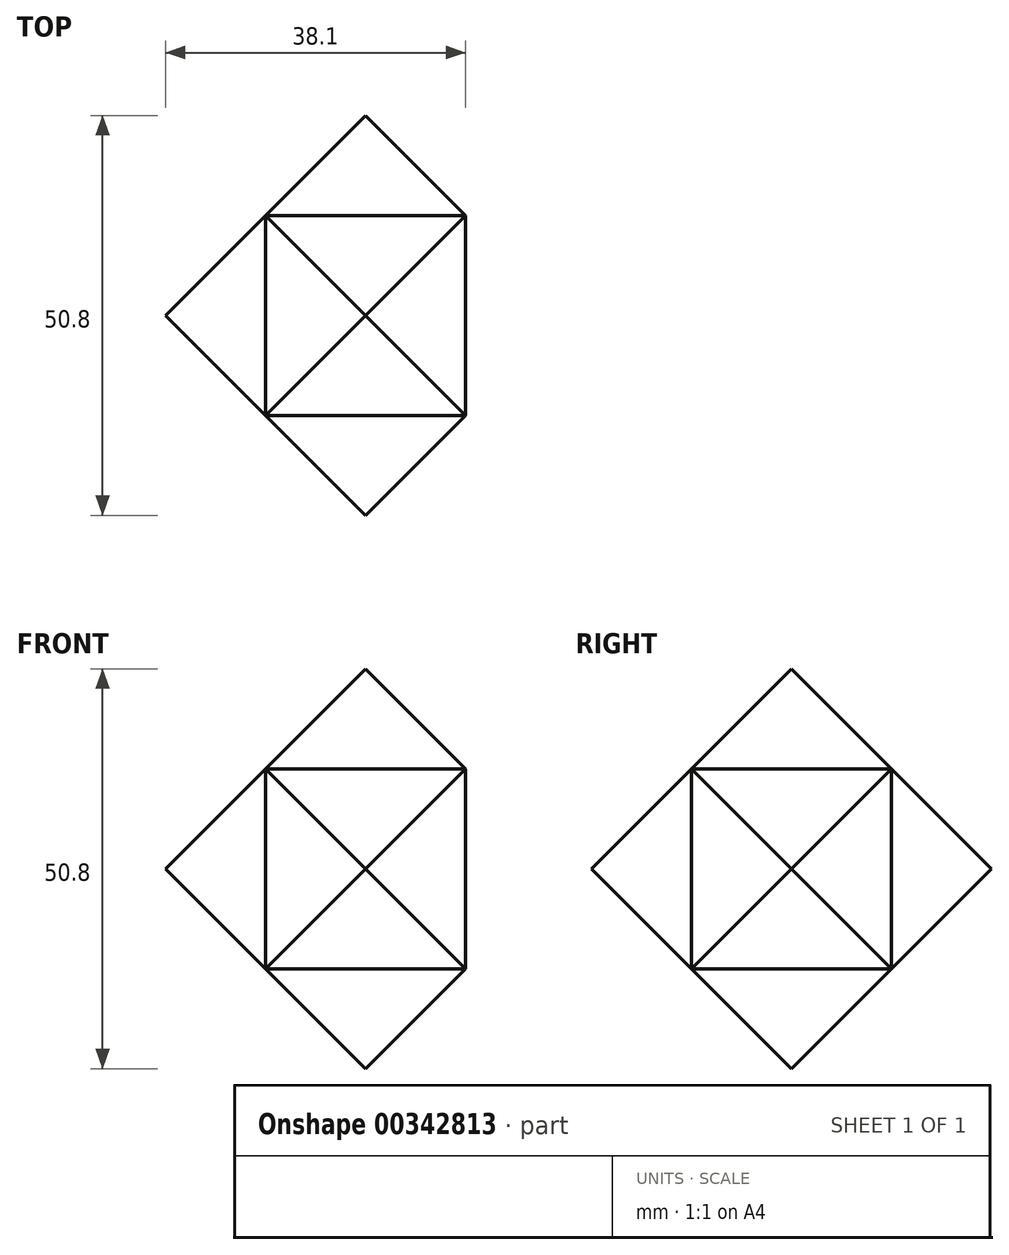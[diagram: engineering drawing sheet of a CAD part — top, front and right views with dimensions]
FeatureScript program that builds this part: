
annotation { "Feature Type Name" : "Feature", "Feature Type Description" : "" }
export const myFeature = defineFeature(function(context is Context, id is Id, definition is map)
    precondition{}
    {
        {
            var Q0;
            Q0=qCreatedBy(makeId("Top.planeOp"),FACE);
            var sketch = newSketch(context, id + "F0", { "sketchPlane" : qUnion([Q0])});
            skLineSegment(sketch, "E0.bottom", {"start": v(12.7, -12.7) * mm, "end": v(-12.7, -12.7) * mm});
            skLineSegment(sketch, "E0.top", {"start": v(12.7, 12.7) * mm, "end": v(-12.7, 12.7) * mm});
            skLineSegment(sketch, "E0.left", {"start": v(12.7, -12.7) * mm, "end": v(12.7, 12.7) * mm});
            skLineSegment(sketch, "E0.right", {"start": v(-12.7, -12.7) * mm, "end": v(-12.7, 12.7) * mm});
            skPoint(sketch, "E0.middle", {"position": v(0, 0) * mm});
            skSolve(sketch);
        }
        {
            var Q0;
            Q0=makeQuery(id+"F0.imprint","IMPRINT",FACE,{"disambiguationData":[TD([[makeQuery(id+"F0.imprint","IMPRINT",EDGE,{"derivedFrom":sQuery(id+"F0.wireOp",EDGE,"E0.bottom")}),-1.0]])]});
            extrude(context, id + "F1", {"entities" : qUnion([Q0]), "endBound" : BoundingType.SYMMETRIC, "depth" : 2.54 * mm});
        }
        {
            var Q0;
            Q0=makeQuery(id+"F1.opExtrude","SWEPT_FACE",FACE,{"disambiguationData":[OSD([sQuery(id+"F0.wireOp",EDGE,"E0.left")])]});
            var sketch = newSketch(context, id + "F2", { "sketchPlane" : qUnion([Q0])});
            skLineSegment(sketch, "E1.bottom", {"start": v(12.7, -12.7) * mm, "end": v(-12.7, -12.7) * mm});
            skLineSegment(sketch, "E1.top", {"start": v(12.7, 12.7) * mm, "end": v(-12.7, 12.7) * mm});
            skLineSegment(sketch, "E1.left", {"start": v(12.7, -12.7) * mm, "end": v(12.7, 12.7) * mm});
            skLineSegment(sketch, "E1.right", {"start": v(-12.7, -12.7) * mm, "end": v(-12.7, 12.7) * mm});
            skPoint(sketch, "E1.middle", {"position": v(0, 0) * mm});
            skSolve(sketch);
        }
        {
            var Q0;
            {var subQ0=sQuery(id+"F2.wireOp",EDGE,"E1.top");Q0=makeQuery(id+"F2.imprint","IMPRINT",FACE,{"disambiguationData":[TD([[makeQuery(id+"F2.imprint","IMPRINT",EDGE,{"derivedFrom":subQ0}),1.0]])]});}
            var Q1;
            {var subQ1=sQuery(id+"F0.wireOp",EDGE,"E0.left");var subQ2=makeQuery(id+"F1.opExtrude","CAP_EDGE",EDGE,{"disambiguationData":[OSD([subQ1])],"isStart":true});Q1=makeQuery(id+"F2.imprint","IMPRINT",FACE,{"disambiguationData":[TD([[makeQuery(id+"F2.imprint","IMPRINT",EDGE,{"derivedFrom":subQ2}),1.0]])]});}
            var Q2;
            {var subQ0=sQuery(id+"F2.wireOp",EDGE,"E1.bottom");Q2=makeQuery(id+"F2.imprint","IMPRINT",FACE,{"disambiguationData":[TD([[makeQuery(id+"F2.imprint","IMPRINT",EDGE,{"derivedFrom":subQ0}),-1.0]])]});}
            var Q3;
            Q3=makeQuery(id+"F1.opExtrude","SWEPT_FACE",FACE,{"disambiguationData":[OSD([sQuery(id+"F0.wireOp",EDGE,"E0.right")])]});
            extrude(context, id + "F3", {"entities" : qUnion([Q0, Q1, Q2]), "operationType" : NewBodyOperationType.ADD, "endBound" : BoundingType.UP_TO_SURFACE, "oppositeDirection" : true, "endBoundEntityFace" : qUnion([Q3]), "depth" : 25.4 * mm});
        }
        {
            var Q0;
            Q0=makeQuery(id+"F3.opExtrude","SWEPT_EDGE",EDGE,{"disambiguationData":[OSD([sQuery(id+"F2.wireOp",EDGE,"E1.top"),sQuery(id+"F2.wireOp",EDGE,"E1.right")])]});
            var Q1;
            {var subQ0=sQuery(id+"F2.wireOp",EDGE,"E1.right");var subQ1=sQuery(id+"F0.wireOp",EDGE,"E0.left");var subQ2=makeQuery(id+"F2.imprint","INTERSECT",VERTEX,{"derivedFrom":[makeQuery(id+"F1.opExtrude","CAP_EDGE",EDGE,{"disambiguationData":[OSD([subQ1])],"isStart":false}),subQ0]});var subQ3=makeQuery(id+"F2.imprint","INTERSECT",VERTEX,{"derivedFrom":[makeQuery(id+"F1.opExtrude","CAP_EDGE",EDGE,{"disambiguationData":[OSD([subQ1])],"isStart":true}),subQ0]});var subQ4=sQuery(id+"F0.wireOp",EDGE,"E0.right");Q1=makeQuery(id+"F3.boolean.opBoolean","MERGE",EDGE,{"derivedFrom":[makeQuery(id+"F1.opExtrude","SWEPT_EDGE",EDGE,{"disambiguationData":[OSD([sQuery(id+"F0.wireOp",EDGE,"E0.bottom"),subQ4])]}),makeQuery(id+"F3.opExtrude","TWEAK_EDGE",EDGE,{"derivedFrom":[makeQuery(id+"F1.opExtrude","SWEPT_FACE",FACE,{"disambiguationData":[OSD([subQ4])]}),makeQuery(id+"F2.imprint","IMPRINT",EDGE,{"disambiguationData":[TD([[subQ3,1.0],[makeQuery(id+"F2.imprint","INTERSECT",VERTEX,{"derivedFrom":[sQuery(id+"F2.wireOp",EDGE,"E1.bottom"),subQ0]}),-1.0]])],"derivedFrom":subQ0}),makeQuery(id+"F2.imprint","IMPRINT",EDGE,{"disambiguationData":[TD([[subQ3,1.0],[subQ2,-1.0]])],"derivedFrom":subQ0}),makeQuery(id+"F2.imprint","IMPRINT",EDGE,{"disambiguationData":[TD([[subQ2,-1.0],[makeQuery(id+"F2.imprint","INTERSECT",VERTEX,{"derivedFrom":[sQuery(id+"F2.wireOp",EDGE,"E1.top"),subQ0]}),1.0]])],"derivedFrom":subQ0})]})]});}
            var Q2;
            Q2=makeQuery(id+"F3.boolean.opBoolean","MERGE",EDGE,{"derivedFrom":[makeQuery(id+"F1.opExtrude","SWEPT_EDGE",EDGE,{"disambiguationData":[OSD([sQuery(id+"F0.wireOp",EDGE,"E0.bottom"),sQuery(id+"F0.wireOp",EDGE,"E0.left")])]}),makeQuery(id+"F3.opExtrude","CAP_EDGE",EDGE,{"disambiguationData":[OSD([sQuery(id+"F2.wireOp",EDGE,"E1.right")])],"isStart":true})]});
            var Q3;
            Q3=makeQuery(id+"F3.boolean.opBoolean","MERGE",EDGE,{"derivedFrom":[makeQuery(id+"F1.opExtrude","SWEPT_EDGE",EDGE,{"disambiguationData":[OSD([sQuery(id+"F0.wireOp",EDGE,"E0.top"),sQuery(id+"F0.wireOp",EDGE,"E0.left")])]}),makeQuery(id+"F3.opExtrude","CAP_EDGE",EDGE,{"disambiguationData":[OSD([sQuery(id+"F2.wireOp",EDGE,"E1.left")])],"isStart":true})]});
            var Q4;
            Q4=makeQuery(id+"F3.opExtrude","SWEPT_EDGE",EDGE,{"disambiguationData":[OSD([sQuery(id+"F2.wireOp",EDGE,"E1.bottom"),sQuery(id+"F2.wireOp",EDGE,"E1.right")])]});
            var Q5;
            Q5=makeQuery(id+"F3.opExtrude","SWEPT_EDGE",EDGE,{"disambiguationData":[OSD([sQuery(id+"F2.wireOp",EDGE,"E1.top"),sQuery(id+"F2.wireOp",EDGE,"E1.left")])]});
            var Q6;
            Q6=makeQuery(id+"F3.opExtrude","SWEPT_EDGE",EDGE,{"disambiguationData":[OSD([sQuery(id+"F2.wireOp",EDGE,"E1.bottom"),sQuery(id+"F2.wireOp",EDGE,"E1.left")])]});
            var Q7;
            {var subQ0=sQuery(id+"F2.wireOp",EDGE,"E1.left");var subQ1=sQuery(id+"F0.wireOp",EDGE,"E0.left");var subQ2=makeQuery(id+"F2.imprint","INTERSECT",VERTEX,{"derivedFrom":[makeQuery(id+"F1.opExtrude","CAP_EDGE",EDGE,{"disambiguationData":[OSD([subQ1])],"isStart":false}),subQ0]});var subQ3=makeQuery(id+"F2.imprint","INTERSECT",VERTEX,{"derivedFrom":[makeQuery(id+"F1.opExtrude","CAP_EDGE",EDGE,{"disambiguationData":[OSD([subQ1])],"isStart":true}),subQ0]});var subQ4=sQuery(id+"F0.wireOp",EDGE,"E0.right");Q7=makeQuery(id+"F3.boolean.opBoolean","MERGE",EDGE,{"derivedFrom":[makeQuery(id+"F1.opExtrude","SWEPT_EDGE",EDGE,{"disambiguationData":[OSD([sQuery(id+"F0.wireOp",EDGE,"E0.top"),subQ4])]}),makeQuery(id+"F3.opExtrude","TWEAK_EDGE",EDGE,{"derivedFrom":[makeQuery(id+"F1.opExtrude","SWEPT_FACE",FACE,{"disambiguationData":[OSD([subQ4])]}),makeQuery(id+"F2.imprint","IMPRINT",EDGE,{"disambiguationData":[TD([[subQ3,1.0],[makeQuery(id+"F2.imprint","INTERSECT",VERTEX,{"derivedFrom":[sQuery(id+"F2.wireOp",EDGE,"E1.bottom"),subQ0]}),-1.0]])],"derivedFrom":subQ0}),makeQuery(id+"F2.imprint","IMPRINT",EDGE,{"disambiguationData":[TD([[subQ3,1.0],[subQ2,-1.0]])],"derivedFrom":subQ0}),makeQuery(id+"F2.imprint","IMPRINT",EDGE,{"disambiguationData":[TD([[subQ2,-1.0],[makeQuery(id+"F2.imprint","INTERSECT",VERTEX,{"derivedFrom":[sQuery(id+"F2.wireOp",EDGE,"E1.top"),subQ0]}),1.0]])],"derivedFrom":subQ0})]})]});}
            chamfer(context, id + "F4", {"entities" : qUnion([Q0, Q1, Q2, Q3, Q4, Q5, Q6, Q7]), "width" : 12.7 * mm, "tangentPropagation" : true});
        }
        {
            var Q0;
            Q0=makeQuery(id+"F1.opExtrude","SWEPT_BODY",BODY,{"disambiguationData":[OSD([sQuery(id+"F0.wireOp",EDGE,"E0.bottom"),sQuery(id+"F0.wireOp",EDGE,"E0.top"),sQuery(id+"F0.wireOp",EDGE,"E0.left"),sQuery(id+"F0.wireOp",EDGE,"E0.right")])]});
            var Q1;
            {var subQ0=sQuery(id+"F2.wireOp",EDGE,"E1.left");Q1=makeQuery(id+"F4.opChamfer","BLEND_EDGE",EDGE,{"blendedFrom":[makeQuery(id+"F3.opExtrude","SWEPT_EDGE",EDGE,{"disambiguationData":[OSD([sQuery(id+"F2.wireOp",EDGE,"E1.top"),subQ0])]}),makeQuery(id+"F3.boolean.opBoolean","MERGE",EDGE,{"derivedFrom":[makeQuery(id+"F1.opExtrude","SWEPT_EDGE",EDGE,{"disambiguationData":[OSD([sQuery(id+"F0.wireOp",EDGE,"E0.top"),sQuery(id+"F0.wireOp",EDGE,"E0.left")])]}),makeQuery(id+"F3.opExtrude","CAP_EDGE",EDGE,{"disambiguationData":[OSD([subQ0])],"isStart":true})]})],"blendedInto":[]});}
            transform(context, id + "F5", {"entities" : qUnion([Q0]), "transformType" : TransformType.ROTATION, "transformAxis" : qUnion([Q1]), "angle" : 120 * degree, "makeCopy" : true});
        }
        {
            var Q0;
            Q0=makeQuery(id+"F1.opExtrude","SWEPT_BODY",BODY,{"disambiguationData":[OSD([sQuery(id+"F0.wireOp",EDGE,"E0.bottom"),sQuery(id+"F0.wireOp",EDGE,"E0.top"),sQuery(id+"F0.wireOp",EDGE,"E0.left"),sQuery(id+"F0.wireOp",EDGE,"E0.right")])]});
            var Q1;
            Q1=makeQuery(id+"F5.opPattern","COPY",BODY,{"derivedFrom":makeQuery(id+"F1.opExtrude","SWEPT_BODY",BODY,{"disambiguationData":[OSD([sQuery(id+"F0.wireOp",EDGE,"E0.bottom"),sQuery(id+"F0.wireOp",EDGE,"E0.top"),sQuery(id+"F0.wireOp",EDGE,"E0.left"),sQuery(id+"F0.wireOp",EDGE,"E0.right")])]}),"instanceName":"1"});
            var Q2;
            {var subQ0=sQuery(id+"F2.wireOp",EDGE,"E1.left");var subQ1=sQuery(id+"F0.wireOp",EDGE,"E0.left");var subQ2=makeQuery(id+"F2.imprint","INTERSECT",VERTEX,{"derivedFrom":[makeQuery(id+"F1.opExtrude","CAP_EDGE",EDGE,{"disambiguationData":[OSD([subQ1])],"isStart":false}),subQ0]});var subQ3=sQuery(id+"F2.wireOp",EDGE,"E1.top");var subQ4=makeQuery(id+"F2.imprint","INTERSECT",VERTEX,{"derivedFrom":[makeQuery(id+"F1.opExtrude","CAP_EDGE",EDGE,{"disambiguationData":[OSD([subQ1])],"isStart":true}),subQ0]});var subQ5=sQuery(id+"F0.wireOp",EDGE,"E0.right");Q2=makeQuery(id+"F5.opPattern","COPY",EDGE,{"derivedFrom":makeQuery(id+"F4.opChamfer","BLEND_EDGE",EDGE,{"blendedFrom":[makeQuery(id+"F3.opExtrude","SWEPT_EDGE",EDGE,{"disambiguationData":[OSD([subQ3,subQ0])]}),makeQuery(id+"F3.boolean.opBoolean","MERGE",EDGE,{"derivedFrom":[makeQuery(id+"F1.opExtrude","SWEPT_EDGE",EDGE,{"disambiguationData":[OSD([sQuery(id+"F0.wireOp",EDGE,"E0.top"),subQ5])]}),makeQuery(id+"F3.opExtrude","TWEAK_EDGE",EDGE,{"derivedFrom":[makeQuery(id+"F1.opExtrude","SWEPT_FACE",FACE,{"disambiguationData":[OSD([subQ5])]}),makeQuery(id+"F2.imprint","IMPRINT",EDGE,{"disambiguationData":[TD([[subQ4,1.0],[makeQuery(id+"F2.imprint","INTERSECT",VERTEX,{"derivedFrom":[sQuery(id+"F2.wireOp",EDGE,"E1.bottom"),subQ0]}),-1.0]])],"derivedFrom":subQ0}),makeQuery(id+"F2.imprint","IMPRINT",EDGE,{"disambiguationData":[TD([[subQ4,1.0],[subQ2,-1.0]])],"derivedFrom":subQ0}),makeQuery(id+"F2.imprint","IMPRINT",EDGE,{"disambiguationData":[TD([[subQ2,-1.0],[makeQuery(id+"F2.imprint","INTERSECT",VERTEX,{"derivedFrom":[subQ3,subQ0]}),1.0]])],"derivedFrom":subQ0})]})]})],"blendedInto":[]}),"instanceName":"1"});}
            transform(context, id + "F6", {"entities" : qUnion([Q0, Q1]), "transformType" : TransformType.ROTATION, "transformAxis" : qUnion([Q2]), "angle" : 120 * degree, "makeCopy" : true});
        }
        {
            var Q0;
            Q0=makeQuery(id+"F1.opExtrude","SWEPT_BODY",BODY,{"disambiguationData":[OSD([sQuery(id+"F0.wireOp",EDGE,"E0.bottom"),sQuery(id+"F0.wireOp",EDGE,"E0.top"),sQuery(id+"F0.wireOp",EDGE,"E0.left"),sQuery(id+"F0.wireOp",EDGE,"E0.right")])]});
            var Q1;
            Q1=makeQuery(id+"F5.opPattern","COPY",BODY,{"derivedFrom":makeQuery(id+"F1.opExtrude","SWEPT_BODY",BODY,{"disambiguationData":[OSD([sQuery(id+"F0.wireOp",EDGE,"E0.bottom"),sQuery(id+"F0.wireOp",EDGE,"E0.top"),sQuery(id+"F0.wireOp",EDGE,"E0.left"),sQuery(id+"F0.wireOp",EDGE,"E0.right")])]}),"instanceName":"1"});
            var Q2;
            Q2=makeQuery(id+"F6.opPattern","COPY",BODY,{"derivedFrom":makeQuery(id+"F1.opExtrude","SWEPT_BODY",BODY,{"disambiguationData":[OSD([sQuery(id+"F0.wireOp",EDGE,"E0.bottom"),sQuery(id+"F0.wireOp",EDGE,"E0.top"),sQuery(id+"F0.wireOp",EDGE,"E0.left"),sQuery(id+"F0.wireOp",EDGE,"E0.right")])]}),"instanceName":"1"});
            var Q3;
            Q3=makeQuery(id+"F6.opPattern","COPY",BODY,{"derivedFrom":makeQuery(id+"F5.opPattern","COPY",BODY,{"derivedFrom":makeQuery(id+"F1.opExtrude","SWEPT_BODY",BODY,{"disambiguationData":[OSD([sQuery(id+"F0.wireOp",EDGE,"E0.bottom"),sQuery(id+"F0.wireOp",EDGE,"E0.top"),sQuery(id+"F0.wireOp",EDGE,"E0.left"),sQuery(id+"F0.wireOp",EDGE,"E0.right")])]}),"instanceName":"1"}),"instanceName":"1"});
            var Q4;
            {var subQ0=sQuery(id+"F2.wireOp",EDGE,"E1.left");Q4=makeQuery(id+"F6.opPattern","COPY",EDGE,{"derivedFrom":makeQuery(id+"F4.opChamfer","BLEND_EDGE",EDGE,{"blendedFrom":[makeQuery(id+"F3.opExtrude","SWEPT_EDGE",EDGE,{"disambiguationData":[OSD([sQuery(id+"F2.wireOp",EDGE,"E1.top"),subQ0])]}),makeQuery(id+"F3.boolean.opBoolean","MERGE",EDGE,{"derivedFrom":[makeQuery(id+"F1.opExtrude","SWEPT_EDGE",EDGE,{"disambiguationData":[OSD([sQuery(id+"F0.wireOp",EDGE,"E0.top"),sQuery(id+"F0.wireOp",EDGE,"E0.left")])]}),makeQuery(id+"F3.opExtrude","CAP_EDGE",EDGE,{"disambiguationData":[OSD([subQ0])],"isStart":true})]})],"blendedInto":[]}),"instanceName":"1"});}
            transform(context, id + "F7", {"entities" : qUnion([Q0, Q1, Q2, Q3]), "transformType" : TransformType.ROTATION, "transformAxis" : qUnion([Q4]), "angle" : 120 * degree, "makeCopy" : true});
        }
    });
